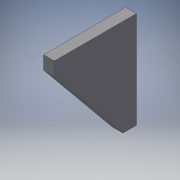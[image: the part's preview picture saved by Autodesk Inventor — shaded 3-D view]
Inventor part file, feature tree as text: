
AUTODESK INVENTOR PART (.ipt)
format: ipt  version: 2018 (Build 220112000, 112)  size: 93,696 bytes
history: native  units: mm
features: extrude x1, sketch x1
ambient origin geometry x8: Origin, YZ Plane, XZ Plane, XY Plane, X Axis, Y Axis, Z Axis, Center Point
bodies: Solido1 (feature_tree)
feature tree (2):
  extrude  "Estrusione1"  Depth=61.0mm
  sketch  "Schizzo1"
